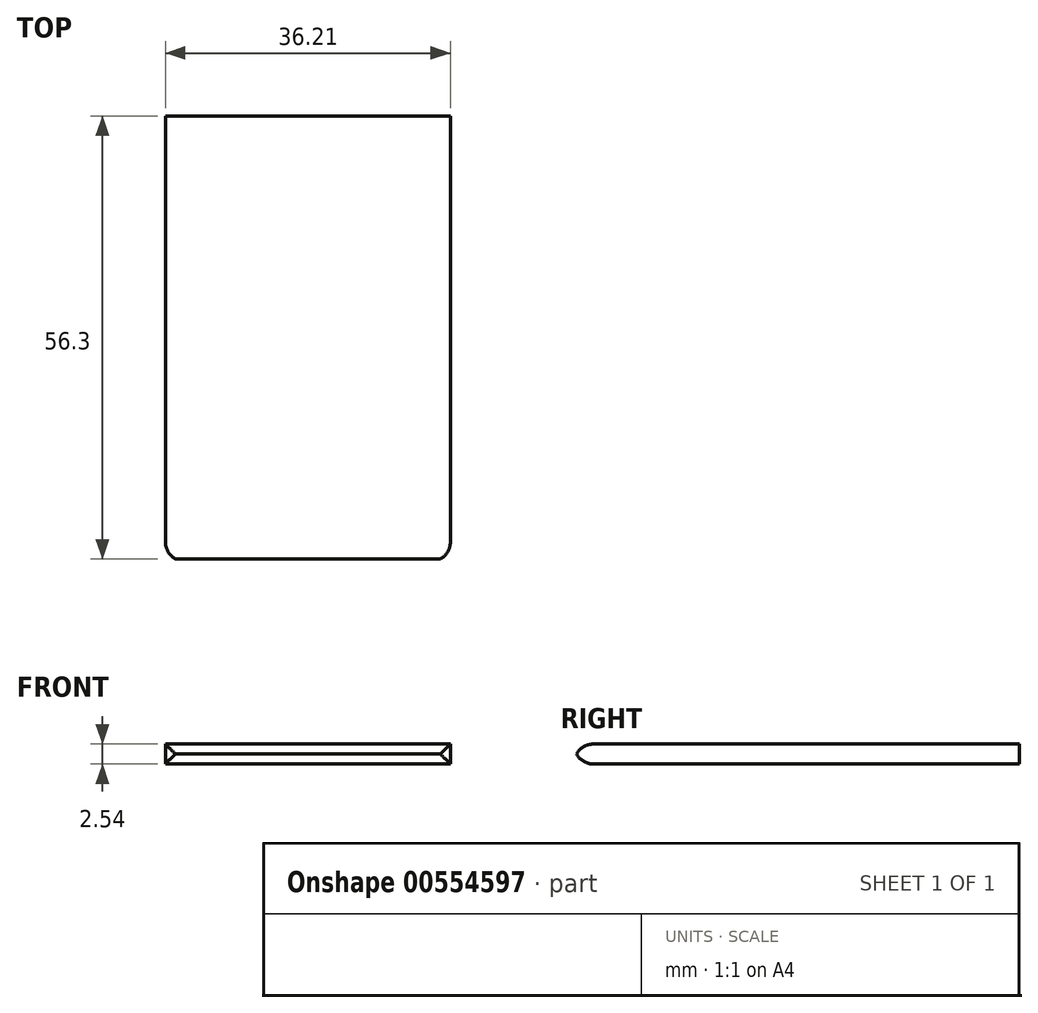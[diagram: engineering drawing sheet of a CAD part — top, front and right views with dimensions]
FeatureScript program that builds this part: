
annotation { "Feature Type Name" : "Feature", "Feature Type Description" : "" }
export const myFeature = defineFeature(function(context is Context, id is Id, definition is map)
    precondition{}
    {
        {
            var Q0;
            Q0=qCreatedBy(makeId("Top.planeOp"),FACE);
            var sketch = newSketch(context, id + "F0", { "sketchPlane" : qUnion([Q0])});
            skLineSegment(sketch, "E0", {"start": v(-120.51, 18) * mm, "end": v(-120.51, -38.65) * mm});
            skLineSegment(sketch, "E1", {"start": v(-120.51, -38.65) * mm, "end": v(-84.3, -38.65) * mm});
            skLineSegment(sketch, "E2", {"start": v(-84.3, -38.65) * mm, "end": v(-84.3, 18) * mm});
            skLineSegment(sketch, "E3", {"start": v(-84.3, 18) * mm, "end": v(-120.51, 18) * mm});
            skSolve(sketch);
        }
        {
            var Q0;
            Q0=makeQuery(id+"F0.imprint","IMPRINT",FACE,{"disambiguationData":[TD([[makeQuery(id+"F0.imprint","IMPRINT",EDGE,{"derivedFrom":sQuery(id+"F0.wireOp",EDGE,"E0")}),1.0]])]});
            extrude(context, id + "F1", {"entities" : qUnion([Q0]), "depth" : 2.54 * mm, "offsetDistance" : 25.4 * mm});
        }
        {
            var Q0;
            Q0=makeQuery(id+"F1.opExtrude","SWEPT_FACE",FACE,{"disambiguationData":[OSD([sQuery(id+"F0.wireOp",EDGE,"E1")])]});
            fillet(context, id + "F2", {"entities" : qUnion([Q0]), "radius" : 2.54 * mm, "tangentPropagation" : true, "allowEdgeOverflow" : false});
        }
    });
